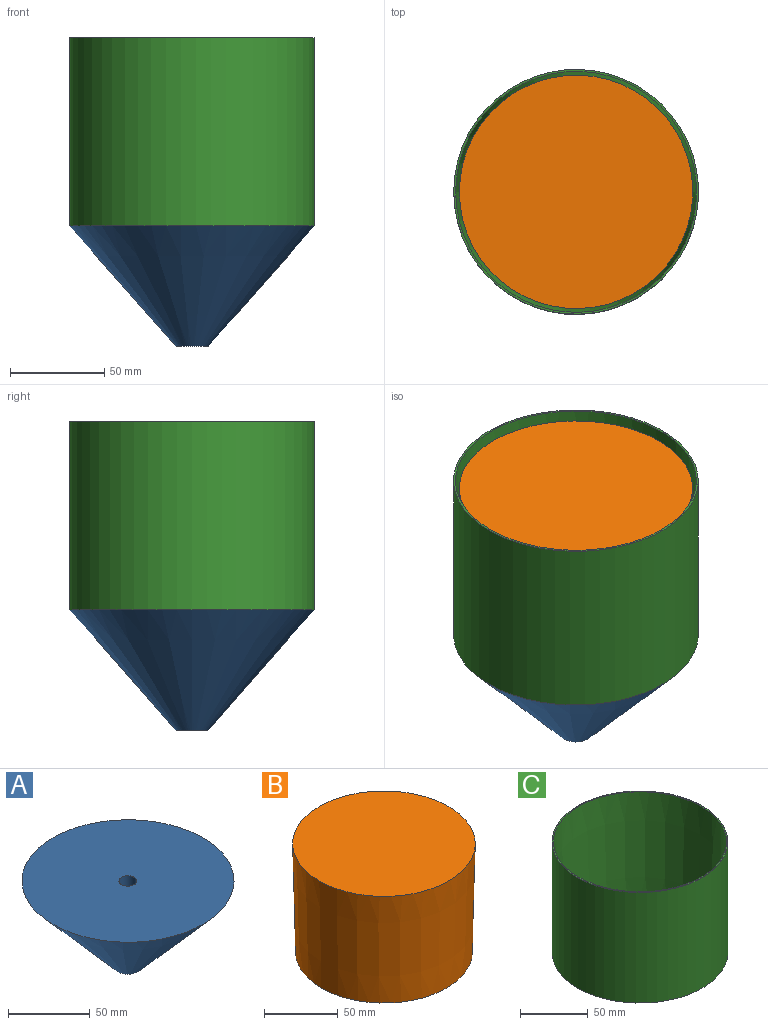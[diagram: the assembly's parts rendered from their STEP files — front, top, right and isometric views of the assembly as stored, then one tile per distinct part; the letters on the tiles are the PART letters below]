
ASSEMBLY  parts=3 mates=2
PART A: 5 faces, bbox 130x130x64 mm
  f0: plane 130x130mm, normal (0,0,1), area 13178.2mm2, adj f1,f4
  f1: cone r=65mm half-angle=41.4deg, axis (0,0,1), area 19712.8mm2, adj f0,f2
  f2: cylinder r=8.5mm len=17mm, axis (0,0,-1), area 587.5mm2, adj f1,f3
  f3: plane 17x17mm, normal (0,0,-1), area 131.9mm2, adj f2,f4
  f4: cylinder r=5.5mm len=53mm, axis (0,0,-1), area 1831.5mm2, adj f0,f3
PART B: 14 faces, bbox 124x124x90 mm
  f0: plane 13x13mm, normal (0,0,-1), area 132.7mm2, adj f10
  f1: plane 124x124mm, normal (0,0,1), area 12076.3mm2, adj f2
  f2: cone r=60mm half-angle=1.3deg, axis (0,0,1), area 34503.2mm2, adj f1,f3
  f3: plane 120x120mm, normal (0,0,-1), area 4948mm2, adj f2,f11
  f4: cylinder r=40mm len=80mm, axis (0,0,-1), area 10053.1mm2, adj f11,f12
  f5: plane 70x70mm, normal (0,0,-1), area 1472.6mm2, adj f12,f13
  f6: cylinder r=22.5mm len=45mm, axis (0,0,-1), area 6361.7mm2, adj f7,f13
  f7: plane 45x45mm, normal (0,0,-1), area 1437.6mm2, adj f6,f8
  f8: cylinder r=6.98mm len=13.95mm, axis (0,0,-1), area 32.9mm2, adj f7,f9
  f9: cone r=6.5mm half-angle=45deg, axis (0,0,-1), area 28.4mm2, adj f8,f10
  f10: cylinder r=6.5mm len=16.38mm, axis (0,0,-1), area 668.8mm2, adj f0,f9
  f11: torus R=45mm, axis (0,0,1), area 2063.6mm2, adj f3,f4
  f12: torus R=35mm, axis (0,0,1), area 1884.3mm2, adj f4,f5
  f13: torus R=27.5mm, axis (0,0,1), area 1200mm2, adj f5,f6
PART C: 4 faces, bbox 130x130x100 mm
  f0: cone r=60mm half-angle=2.3deg, axis (0,0,1), area 38986.9mm2, adj f1,f3
  f1: plane 130x130mm, normal (0,0,-1), area 1963.5mm2, adj f0,f2
  f2: cylinder r=65mm len=130mm, axis (0,0,-1), area 40840.7mm2, adj f1,f3
  f3: plane 130x130mm, normal (0,0,1), area 405.3mm2, adj f0,f2
PLACE A t=(-133.75,-0.1,-18.97)mm
PLACE B t=(-133.75,-0.1,-18.97)mm
PLACE C t=(-133.75,-0.1,-18.97)mm
MATE slider B.f2 <-> C.f0  axis (0,0,1) through (-133.75,-0.1,26.03)mm
MATE planar C.f0 <-> A.f1  axis (0,0,-1) through (-133.75,-0.1,-23.97)mm
